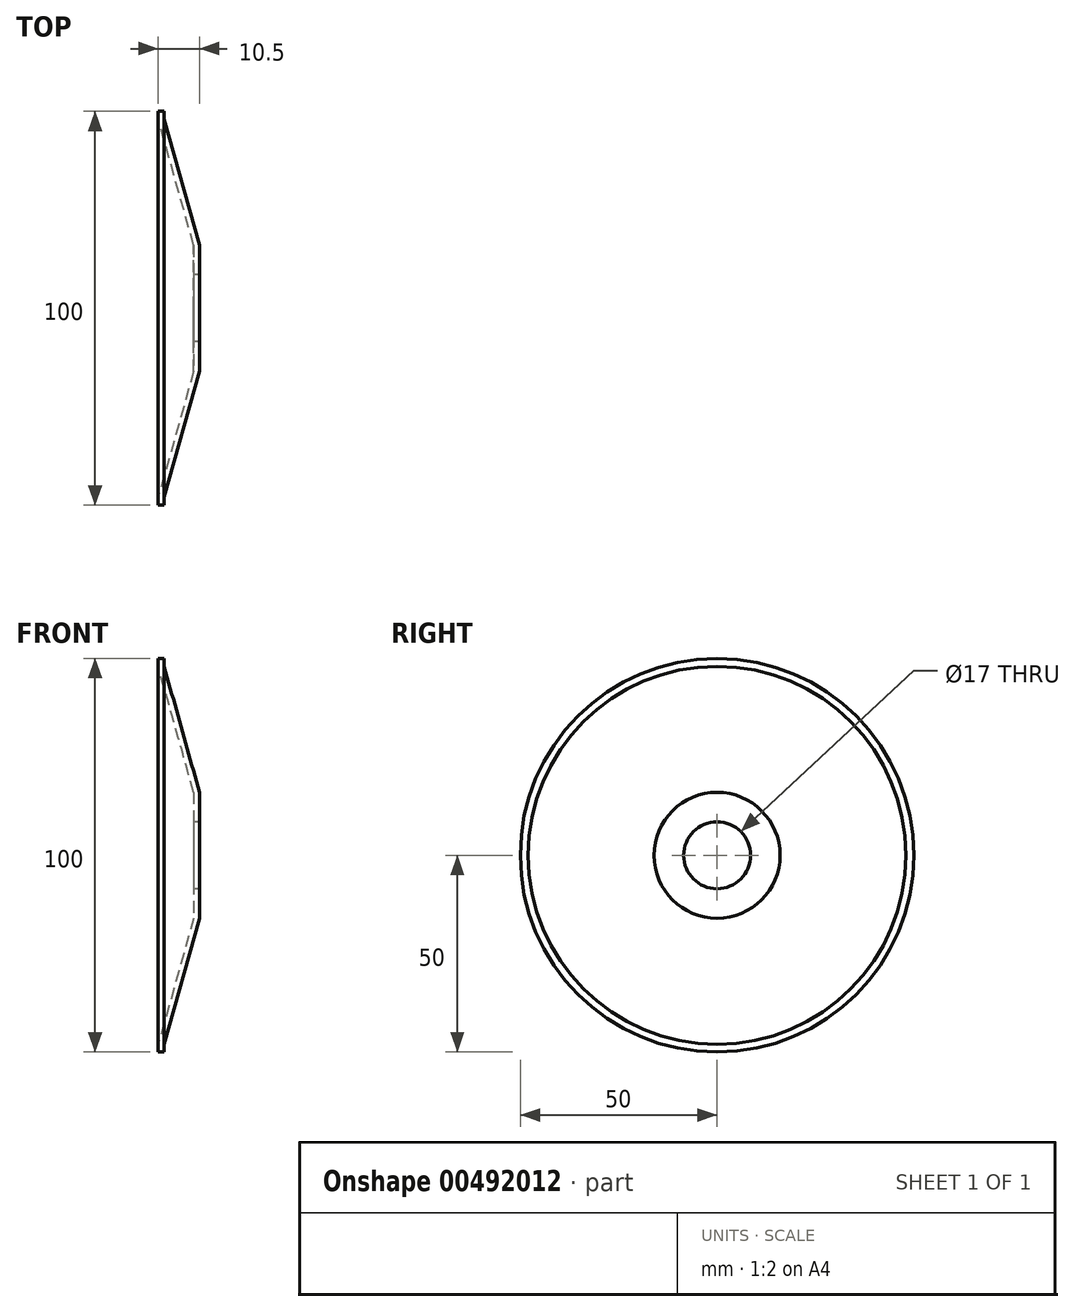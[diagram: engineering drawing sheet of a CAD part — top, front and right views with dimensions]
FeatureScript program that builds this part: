
annotation { "Feature Type Name" : "Feature", "Feature Type Description" : "" }
export const myFeature = defineFeature(function(context is Context, id is Id, definition is map)
    precondition{}
    {
        {
            var Q0;
            Q0=qCreatedBy(makeId("Front.planeOp"),FACE);
            var sketch = newSketch(context, id + "F0", { "sketchPlane" : qUnion([Q0])});
            skLineSegment(sketch, "E0", {"start": v(24, 8.5) * mm, "end": v(24, 16) * mm});
            skLineSegment(sketch, "E1", {"start": v(15, 48) * mm, "end": v(15, 50) * mm});
            skLineSegment(sketch, "E2", {"start": v(25.5, 16) * mm, "end": v(25.5, 8.5) * mm});
            skLineSegment(sketch, "E3", {"start": v(25.5, 8.5) * mm, "end": v(24, 8.5) * mm});
            skLineSegment(sketch, "E4", {"start": v(19.28, 0) * mm, "end": v(42.08, 0) * mm, "construction": true});
            skLineSegment(sketch, "E5", {"start": v(16.5, 48) * mm, "end": v(16.5, 50) * mm});
            skLineSegment(sketch, "E6", {"start": v(16.5, 50) * mm, "end": v(15, 50) * mm});
            skLineSegment(sketch, "E7", {"start": v(15, 48) * mm, "end": v(24, 16) * mm});
            skLineSegment(sketch, "E8", {"start": v(16.5, 48) * mm, "end": v(25.5, 16) * mm});
            skSolve(sketch);
        }
        {
            var Q0;
            Q0=makeQuery(id+"F0.imprint","IMPRINT",FACE,{"disambiguationData":[TD([[makeQuery(id+"F0.imprint","IMPRINT",EDGE,{"derivedFrom":sQuery(id+"F0.wireOp",EDGE,"E0")}),-1.0]])]});
            var Q1;
            Q1=sQuery(id+"F0.wireOp",EDGE,"E4");
            revolve(context, id + "F1", {"entities" : qUnion([Q0]), "axis" : qUnion([Q1]), "revolveType" : RevolveType.FULL});
        }
    });
